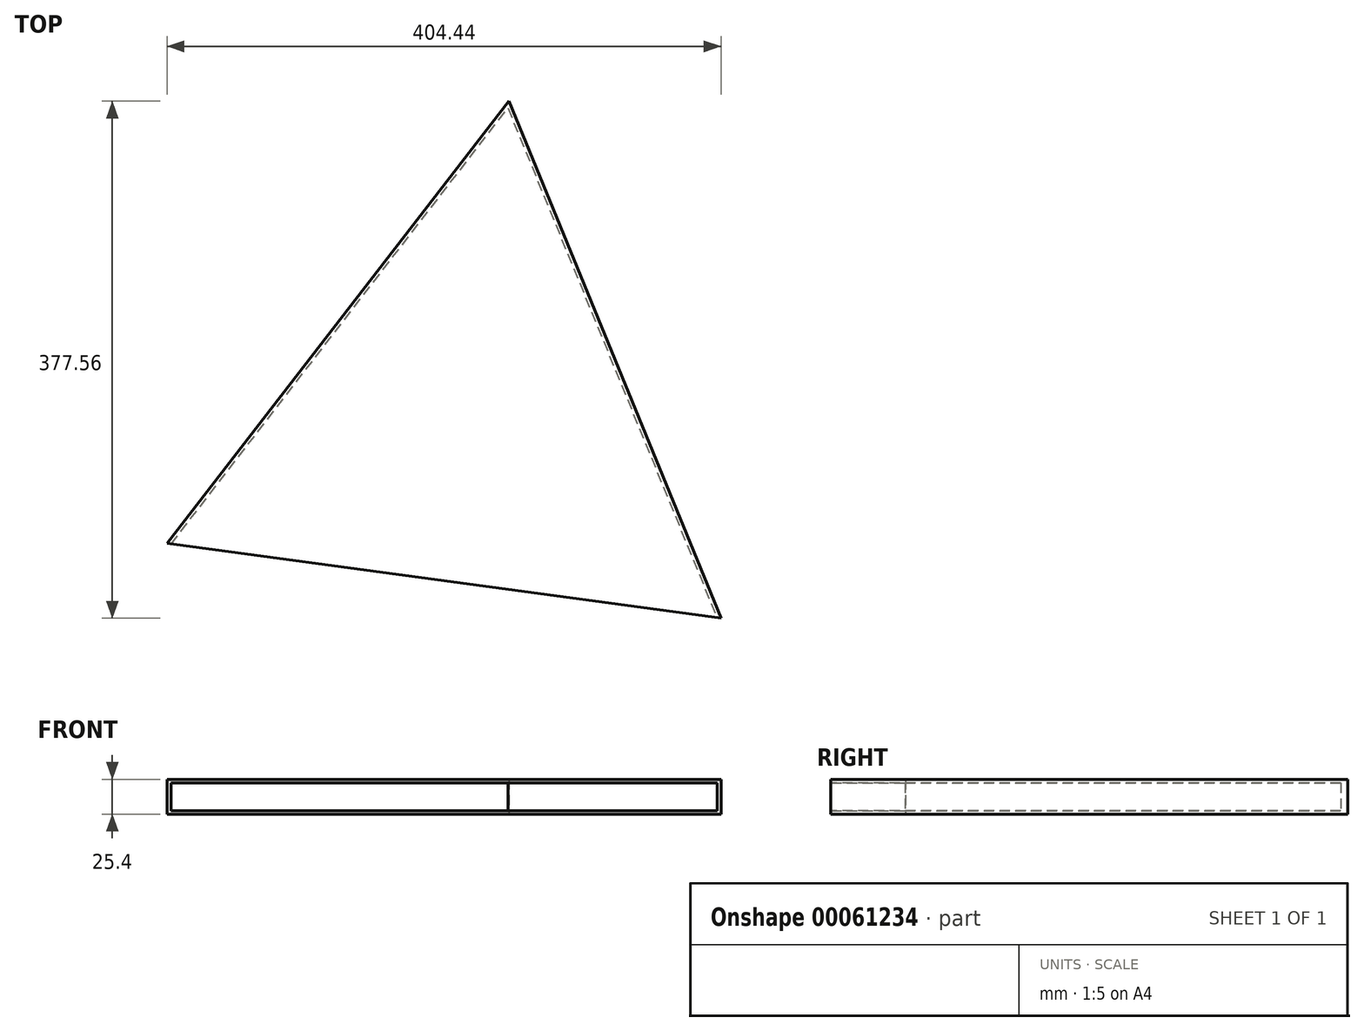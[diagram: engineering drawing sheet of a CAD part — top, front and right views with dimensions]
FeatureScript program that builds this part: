
annotation { "Feature Type Name" : "Feature", "Feature Type Description" : "" }
export const myFeature = defineFeature(function(context is Context, id is Id, definition is map)
    precondition{}
    {
        {
            var Q0;
            Q0=qCreatedBy(makeId("Top.planeOp"),FACE);
            var sketch = newSketch(context, id + "F0", { "sketchPlane" : qUnion([Q0])});
            skCircle(sketch, "E0.cCircle", {"center": v(0, 0) * mm, "radius": 117.81 * mm, "construction": true});
            skLineSegment(sketch, "E0.0", {"start": v(31.54, 233.5) * mm, "end": v(186.45, -144.06) * mm});
            skLineSegment(sketch, "E0.1", {"start": v(186.45, -144.06) * mm, "end": v(-217.99, -89.44) * mm});
            skLineSegment(sketch, "E0.2", {"start": v(-217.99, -89.44) * mm, "end": v(31.54, 233.5) * mm});
            skPoint(sketch, "E0.0.midPoint", {"position": v(109, 44.72) * mm});
            skSolve(sketch);
        }
        {
            var Q0;
            Q0=makeQuery(id+"F0.imprint","IMPRINT",FACE,{"disambiguationData":[TD([[makeQuery(id+"F0.imprint","IMPRINT",EDGE,{"derivedFrom":sQuery(id+"F0.wireOp",EDGE,"E0.0")}),-1.0]])]});
            extrude(context, id + "F1", {"entities" : qUnion([Q0]), "depth" : 25.4 * mm});
        }
        {
            var Q0;
            Q0=makeQuery(id+"F1.opExtrude","SWEPT_FACE",FACE,{"disambiguationData":[OSD([sQuery(id+"F0.wireOp",EDGE,"E0.1")])]});
            shell(context, id + "F2", {"entities" : qUnion([Q0]), "thickness" : 2.54 * mm});
        }
    });
